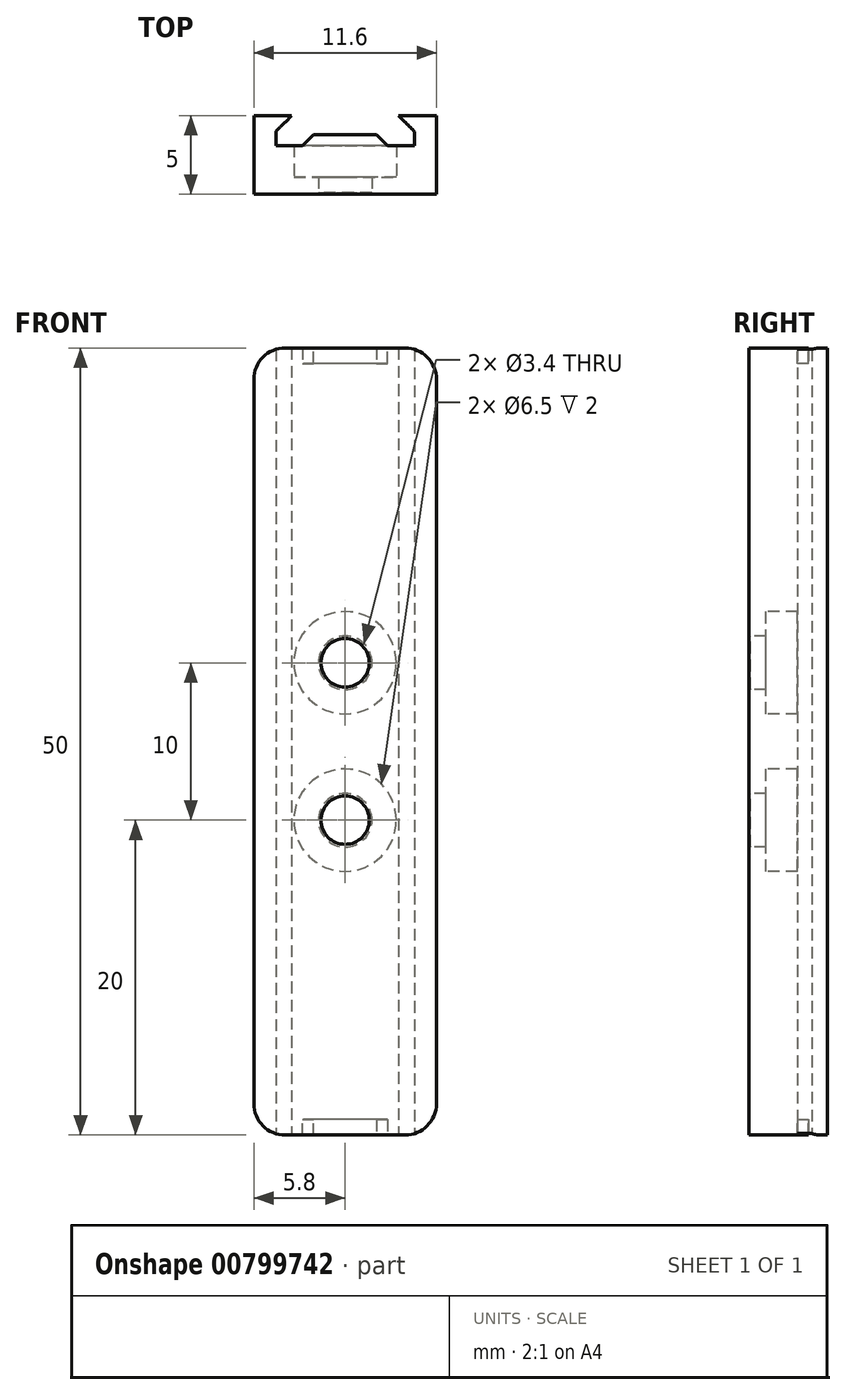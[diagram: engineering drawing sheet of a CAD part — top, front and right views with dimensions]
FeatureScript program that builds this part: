
annotation { "Feature Type Name" : "Feature", "Feature Type Description" : "" }
export const myFeature = defineFeature(function(context is Context, id is Id, definition is map)
    precondition{}
    {
        {
            var Q0;
            Q0=qCreatedBy(makeId("Top.planeOp"),FACE);
            var sketch = newSketch(context, id + "F0", { "sketchPlane" : qUnion([Q0])});
            skLineSegment(sketch, "E0.bottom", {"start": v(5.8, -2.5) * mm, "end": v(-5.8, -2.5) * mm});
            skLineSegment(sketch, "E0.top", {"start": v(5.8, 2.5) * mm, "end": v(-5.8, 2.5) * mm});
            skLineSegment(sketch, "E0.left", {"start": v(5.8, -2.5) * mm, "end": v(5.8, 2.5) * mm});
            skLineSegment(sketch, "E0.right", {"start": v(-5.8, -2.5) * mm, "end": v(-5.8, 2.5) * mm});
            skPoint(sketch, "E0.middle", {"position": v(0, 0) * mm});
            skPoint(sketch, "E1", {"position": v(3.4, 2.5) * mm});
            skPoint(sketch, "E2", {"position": v(-3.4, 2.5) * mm});
            skPoint(sketch, "E3", {"position": v(-3.4, 1.5) * mm});
            skPoint(sketch, "E4", {"position": v(3.4, 1.5) * mm});
            skPoint(sketch, "E5", {"position": v(4.4, 1.5) * mm});
            skPoint(sketch, "E6", {"position": v(4.4, 0.6) * mm});
            skPoint(sketch, "E7", {"position": v(-4.4, 0.6) * mm});
            skPoint(sketch, "E8", {"position": v(-4.4, 1.5) * mm});
            skLineSegment(sketch, "E9", {"start": v(-3.4, 2.5) * mm, "end": v(-3.4, 1.5) * mm});
            skLineSegment(sketch, "E10", {"start": v(-3.4, 1.5) * mm, "end": v(-4.4, 1.5) * mm});
            skLineSegment(sketch, "E11", {"start": v(-4.4, 1.5) * mm, "end": v(-4.4, 0.6) * mm});
            skLineSegment(sketch, "E12", {"start": v(-4.4, 0.6) * mm, "end": v(4.4, 0.6) * mm});
            skLineSegment(sketch, "E13", {"start": v(4.4, 0.6) * mm, "end": v(4.4, 1.5) * mm});
            skLineSegment(sketch, "E14", {"start": v(4.4, 1.5) * mm, "end": v(3.4, 1.5) * mm});
            skLineSegment(sketch, "E15", {"start": v(3.4, 1.5) * mm, "end": v(3.4, 2.5) * mm});
            skSolve(sketch);
        }
        {
            var Q0;
            Q0=makeQuery(id+"F0.imprint","IMPRINT",FACE,{"disambiguationData":[TD([[makeQuery(id+"F0.imprint","IMPRINT",EDGE,{"derivedFrom":sQuery(id+"F0.wireOp",EDGE,"E0.bottom")}),-1.0]])]});
            extrude(context, id + "F1", {"entities" : qUnion([Q0]), "depth" : 50 * mm, "offsetDistance" : 25 * mm});
        }
        {
            var Q0;
            Q0=makeQuery(id+"F1.opExtrude","SWEPT_FACE",FACE,{"disambiguationData":[OSD([sQuery(id+"F0.wireOp",EDGE,"E12")])]});
            var sketch = newSketch(context, id + "F2", { "sketchPlane" : qUnion([Q0])});
            skPoint(sketch, "E16", {"position": v(0, 25) * mm});
            skPoint(sketch, "E16.positionSnap0", {"position": v(4.4, 25) * mm});
            skPoint(sketch, "E16.positionSnap1", {"position": v(0, 50) * mm});
            skPoint(sketch, "E17", {"position": v(0, 30) * mm});
            skPoint(sketch, "E18", {"position": v(0, 20) * mm});
            skPoint(sketch, "E19", {"position": v(3, 50) * mm});
            skPoint(sketch, "E20", {"position": v(3, 49) * mm});
            skPoint(sketch, "E21", {"position": v(-3, 50) * mm});
            skPoint(sketch, "E22", {"position": v(-3, 49) * mm});
            skLineSegment(sketch, "E23", {"start": v(-3, 50) * mm, "end": v(-3, 49) * mm});
            skLineSegment(sketch, "E24", {"start": v(-3, 49) * mm, "end": v(3, 49) * mm});
            skLineSegment(sketch, "E25", {"start": v(3, 49) * mm, "end": v(3, 50) * mm});
            skPoint(sketch, "E26", {"position": v(3, 0) * mm});
            skPoint(sketch, "E27", {"position": v(-3, 0) * mm});
            skPoint(sketch, "E28", {"position": v(3, 1) * mm});
            skPoint(sketch, "E29", {"position": v(-3, 1) * mm});
            skLineSegment(sketch, "E30", {"start": v(-3, 0) * mm, "end": v(-3, 1) * mm});
            skLineSegment(sketch, "E31", {"start": v(-3, 1) * mm, "end": v(3, 1) * mm});
            skLineSegment(sketch, "E32", {"start": v(3, 1) * mm, "end": v(3, 0) * mm});
            skSolve(sketch);
        }
        {
            var Q0;
            Q0=sQuery(id+"F2.wireOp",VERTEX,"E17");
            var Q1;
            Q1=sQuery(id+"F2.wireOp",VERTEX,"E18");
            var Q2;
            Q2=makeQuery(id+"F1.opExtrude","SWEPT_BODY",BODY,{"disambiguationData":[OSD([sQuery(id+"F0.wireOp",EDGE,"E0.bottom"),sQuery(id+"F0.wireOp",EDGE,"E0.top"),sQuery(id+"F0.wireOp",EDGE,"E0.left"),sQuery(id+"F0.wireOp",EDGE,"E0.right"),sQuery(id+"F0.wireOp",EDGE,"E9"),sQuery(id+"F0.wireOp",EDGE,"E10"),sQuery(id+"F0.wireOp",EDGE,"E11"),sQuery(id+"F0.wireOp",EDGE,"E12"),sQuery(id+"F0.wireOp",EDGE,"E13"),sQuery(id+"F0.wireOp",EDGE,"E14"),sQuery(id+"F0.wireOp",EDGE,"E15")])]});
            hole(context, id + "F3", {"style" : HoleStyle.C_BORE, "endStyle" : HoleEndStyle.BLIND, "holeDiameter" : 3.4 * mm, "cBoreDiameter" : 6.5 * mm, "cBoreDepth" : 2 * mm, "majorDiameter" : 5 * mm, "holeDepth" : 3 * mm, "isTappedThrough" : true, "tappedDepth" : 12 * mm, "tapClearance" : 3, "startFromSketch" : true, "locations" : qUnion([Q0, Q1]), "scope" : qUnion([Q2])});
        }
        {
            var Q0;
            {var subQ0=sQuery(id+"F2.wireOp",EDGE,"E23");Q0=makeQuery(id+"F2.imprint","IMPRINT",FACE,{"disambiguationData":[TD([[makeQuery(id+"F2.imprint","IMPRINT",EDGE,{"derivedFrom":subQ0}),1.0]])]});}
            var Q1;
            {var subQ0=sQuery(id+"F2.wireOp",EDGE,"E30");Q1=makeQuery(id+"F2.imprint","IMPRINT",FACE,{"disambiguationData":[TD([[makeQuery(id+"F2.imprint","IMPRINT",EDGE,{"derivedFrom":subQ0}),-1.0]])]});}
            extrude(context, id + "F4", {"entities" : qUnion([Q0, Q1]), "operationType" : NewBodyOperationType.ADD, "depth" : 0.7 * mm, "offsetDistance" : 25 * mm});
        }
        {
            var Q0;
            Q0=makeQuery(id+"F1.opExtrude","SWEPT_EDGE",EDGE,{"disambiguationData":[OSD([sQuery(id+"F0.wireOp",EDGE,"E14"),sQuery(id+"F0.wireOp",EDGE,"E15")])]});
            var Q1;
            Q1=makeQuery(id+"F1.opExtrude","SWEPT_EDGE",EDGE,{"disambiguationData":[OSD([sQuery(id+"F0.wireOp",EDGE,"E9"),sQuery(id+"F0.wireOp",EDGE,"E10")])]});
            var Q2;
            Q2=makeQuery(id+"F4.opExtrude","CAP_EDGE",EDGE,{"disambiguationData":[OSD([sQuery(id+"F2.wireOp",EDGE,"E32")])],"isStart":false});
            var Q3;
            Q3=makeQuery(id+"F4.opExtrude","CAP_EDGE",EDGE,{"disambiguationData":[OSD([sQuery(id+"F2.wireOp",EDGE,"E30")])],"isStart":false});
            var Q4;
            Q4=makeQuery(id+"F4.opExtrude","CAP_EDGE",EDGE,{"disambiguationData":[OSD([sQuery(id+"F2.wireOp",EDGE,"E23")])],"isStart":false});
            var Q5;
            Q5=makeQuery(id+"F4.opExtrude","CAP_EDGE",EDGE,{"disambiguationData":[OSD([sQuery(id+"F2.wireOp",EDGE,"E25")])],"isStart":false});
            chamfer(context, id + "F5", {"entities" : qUnion([Q0, Q1, Q2, Q3, Q4, Q5]), "width" : 1 * mm, "tangentPropagation" : true});
        }
        {
            var Q0;
            Q0=makeQuery(id+"F1.opExtrude","CAP_EDGE",EDGE,{"disambiguationData":[OSD([sQuery(id+"F0.wireOp",EDGE,"E0.left")])],"isStart":false});
            var Q1;
            Q1=makeQuery(id+"F1.opExtrude","CAP_EDGE",EDGE,{"disambiguationData":[OSD([sQuery(id+"F0.wireOp",EDGE,"E0.right")])],"isStart":false});
            var Q2;
            Q2=makeQuery(id+"F1.opExtrude","CAP_EDGE",EDGE,{"disambiguationData":[OSD([sQuery(id+"F0.wireOp",EDGE,"E0.right")])],"isStart":true});
            var Q3;
            Q3=makeQuery(id+"F1.opExtrude","CAP_EDGE",EDGE,{"disambiguationData":[OSD([sQuery(id+"F0.wireOp",EDGE,"E0.left")])],"isStart":true});
            fillet(context, id + "F6", {"entities" : qUnion([Q0, Q1, Q2, Q3]), "tangentPropagation" : true, "radius" : 2 * mm, "defaultsChanged" : false, "vertexSettings" : [], "allowEdgeOverflow" : false});
        }
    });
